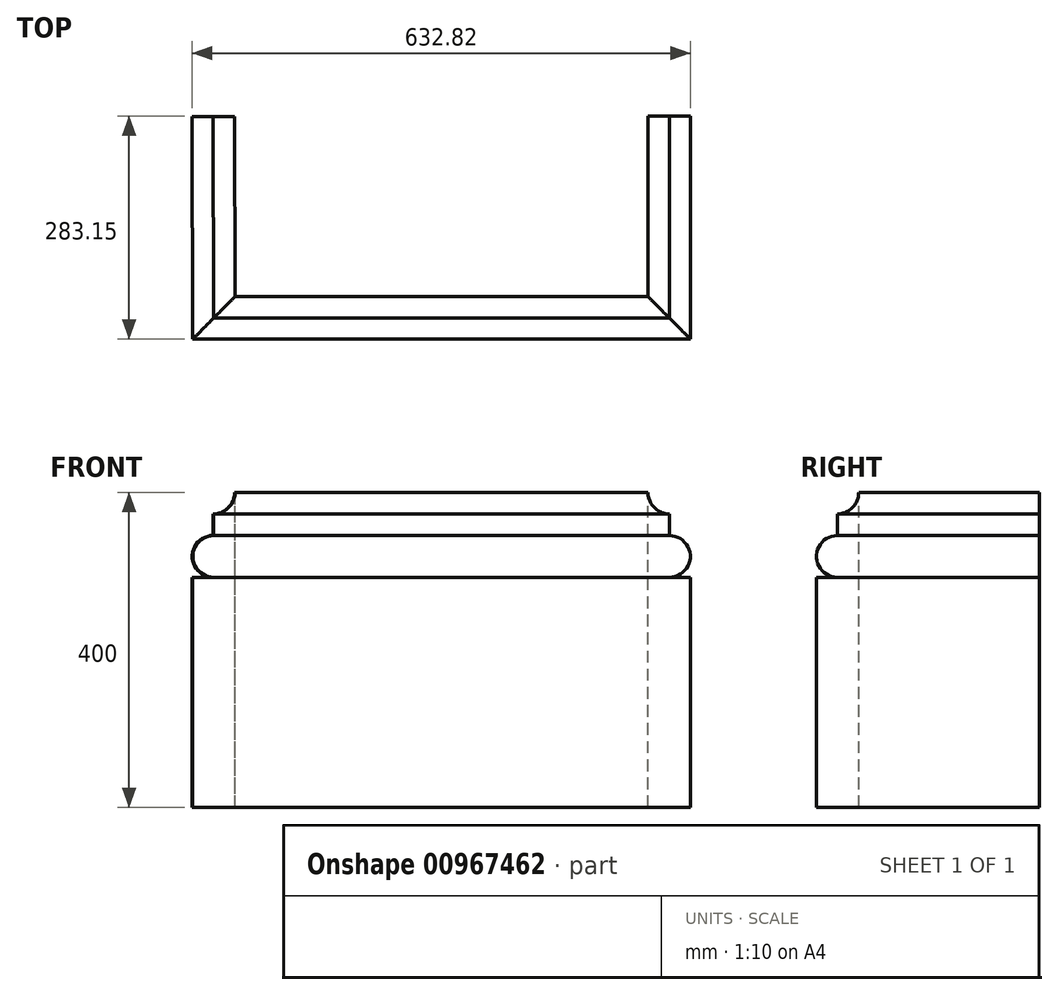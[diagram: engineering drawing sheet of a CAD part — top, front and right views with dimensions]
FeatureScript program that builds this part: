
annotation { "Feature Type Name" : "Feature", "Feature Type Description" : "" }
export const myFeature = defineFeature(function(context is Context, id is Id, definition is map)
    precondition{}
    {
        {
            var Q0;
            Q0=qCreatedBy(makeId("Front.planeOp"),FACE);
            var sketch = newSketch(context, id + "F0", { "sketchPlane" : qUnion([Q0])});
            skLineSegment(sketch, "E0", {"start": v(197.32, 92.34) * mm, "end": v(223.83, 92.34) * mm});
            skLineSegment(sketch, "E1", {"start": v(223.83, -200) * mm, "end": v(223.83, 92.34) * mm});
            skLineSegment(sketch, "E2", {"start": v(197.32, 172.68) * mm, "end": v(197.32, 145.37) * mm});
            skArc(sketch, "E3", {"start": v(197.32, 92.34) * mm, "mid": v(223.83, 118.85) * mm, "end": v(197.32, 145.37) * mm});
            skArc(sketch, "E4", {"start": v(170, 200) * mm, "mid": v(178, 180.68) * mm, "end": v(197.32, 172.68) * mm});
            skLineSegment(sketch, "E5", {"start": v(170, 200) * mm, "end": v(170, -200) * mm});
            skLineSegment(sketch, "E6", {"start": v(170, -200) * mm, "end": v(223.83, -200) * mm});
            skSolve(sketch);
        }
        {
            var Q0;
            Q0=qCreatedBy(makeId("Top.planeOp"),FACE);
            var sketch = newSketch(context, id + "F1", { "sketchPlane" : qUnion([Q0])});
            skLineSegment(sketch, "E7", {"start": v(131.5, -98.5) * mm, "end": v(131.5, 92.33) * mm});
            skLineSegment(sketch, "E8", {"start": v(-316.16, -98.5) * mm, "end": v(-316.67, 91.9) * mm});
            skLineSegment(sketch, "E9", {"start": v(131.5, -98.5) * mm, "end": v(-316.16, -98.5) * mm});
            skSolve(sketch);
        }
        {
            var Q0;
            Q0 = qSketchRegion(id + "F0", true);
            var Q1;
            Q1 = qConstructionFilter(qBodyType(qCreatedBy(id + "F1" ,EDGE), BodyType.WIRE), ConstructionObject.NO);
            sweep(context, id + "F2", {"profiles" : qUnion([Q0]), "path" : qUnion([Q1])});
        }
        {
            var Q0;
            Q0=qCreatedBy(makeId("Top.planeOp"),FACE);
            var sketch = newSketch(context, id + "F3", { "sketchPlane" : qUnion([Q0])});
            skLineSegment(sketch, "E10.bottom", {"start": v(-281.84, 104.4) * mm, "end": v(58.16, 104.4) * mm});
            skLineSegment(sketch, "E10.top", {"start": v(-281.84, 294.4) * mm, "end": v(58.16, 294.4) * mm});
            skLineSegment(sketch, "E10.left", {"start": v(-281.84, 104.4) * mm, "end": v(-281.84, 294.4) * mm});
            skLineSegment(sketch, "E10.right", {"start": v(58.16, 104.4) * mm, "end": v(58.16, 294.4) * mm});
            skSolve(sketch);
        }
        {
            var Q0;
            Q0=sQuery(id+"F3.wireOp",EDGE,"E10.top");
            var Q1;
            Q1=sQuery(id+"F3.wireOp",EDGE,"E10.right");
            var Q2;
            Q2=sQuery(id+"F3.wireOp",EDGE,"E10.bottom");
            var Q3;
            Q3=sQuery(id+"F3.wireOp",EDGE,"E10.left");
            extrude(context, id + "F4", {"bodyType" : ToolBodyType.SURFACE, "surfaceEntities" : qUnion([Q0, Q1, Q2, Q3]), "depth" : 400 * mm, "offsetDistance" : 25 * mm});
        }
    });
